# Revit family: Reece_Laundry Trough_Posh_Domaine_Laundry Trough & Cabinet_27 ltr
name_source: partatom
category: Plumbing Fixtures
revit_build: Autodesk Revit 2018 (Build: 20180329_1100(x64)
units: mm (PartAtom-declared; Revit-internal decimal feet)

## family parameters
Always vertical = Yes
Cut with Voids When Loaded = No
Part Type = Normal
Room Calculation Point = Yes
Round Connector Dimension = Use Diameter
Shared = Yes
Work Plane-Based = No

## types (1)
- 2 Taphole_with Bypass_Stainless Steel_White
    Description = Reece_Laundry Trough_Posh_Domaine_Laundry Trough & Cabinet_27 ltr
    Disclaimer = THIS FILE IS THE PROPERTY OF THE REECE GROUP. IT MAY NOT BE REPRODUCED, REVERSE-ENGINEERED OR MODIFIED. ANY REPUBLICATION, TRANSMISSION OR DISTRIBUTION FOR THE PURPOSE OF COMMERCIALLY EXPLOITING THE FILES IS PROHIBITED.
    Keynote = Product #2409006, Reece_Laundry Trough_Posh_Domaine_Laundry Trough & Cabinet_27 ltr - 2 Taphole_with Bypass_Stainless Steel_White
    Manufacturer = Posh
    Model = Domaine
    Reece_Detail_Additional = Standard Trough
    Reece_Detail_Disclaimer = THIS FILE IS THE PROPERTY OF THE REECE GROUP. IT MAY NOT BE REPRODUCED, REVERSE-ENGINEERED OR MODIFIED. ANY REPUBLICATION, TRANSMISSION OR DISTRIBUTION FOR THE PURPOSE OF COMMERCIALLY EXPLOITING THE FILES IS PROHIBITED.
    Reece_Material-Cabinet = Reece_Acrylic_White
    Reece_Material_Main = Reece_Metal_Steel
    Reece_Material_Secondary = Reece_Metal_Steel
    Reece_Overall_Capacity = 27 L
    Reece_Overall_Height = 880 mm
    Reece_Overall_Length = 570 mm  [stored 1.87008 ft]
    Reece_Overall_Width = 400 mm  [stored 1.31234 ft]
    Reece_Product_Brand = Posh
    Reece_Product_Description = Posh Domaine Trough & Cabinet 27L with Bypass 2 Taphole Stainless Steel
    Reece_Product_Doors = 1
    Reece_Product_Mount = Floor Mounted
    Reece_Product_Number = 2409006
    Reece_Product_Sub Brand = Domaine
    Reece_Product_Web Page = https://www.reece.com.au
    Reece_Sink_Outlet = 40 mm  [stored 0.131234 ft]
    URL = https://www.reece.com.au

note: [stored X ft] marks values corroborated as IEEE doubles in the binary element streams (Revit-internal decimal feet)

## geometry (parser evidence)
native form markers: Sweep x6
no freeform markers — native parametric forms only
